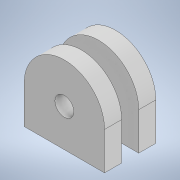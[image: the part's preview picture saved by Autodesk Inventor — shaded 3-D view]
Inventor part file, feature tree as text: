
AUTODESK INVENTOR PART (.ipt)
format: ipt  version: 2021 (Build 250183000, 183)  size: 118,784 bytes
history: native  units: mm
features: plane x2, extrude x1, mirror x1, sketch x1
ambient origin geometry x8: Origin, YZ Plane, XZ Plane, XY Plane, X Axis, Y Axis, Z Axis, Center Point
bodies: Solid1 (feature_tree)
feature tree (5):
  extrude  "Extrusion1"  Depth=10.0mm
  plane  "Work Plane1"
  mirror  "Mirror1"
  plane  "Work Plane2"
  sketch  "Sketch1"  dims[d0=11.0mm d1=18.0mm d2=18.0mm d3=22.0mm d4=90.0deg d5=10.0mm d6=1.0mm d7=0.0mm d8=0.0mm d11=5.0mm d12=0.0mm d17=0.5mm d18=0.872665mm d19=0.5mm d20=0.872665mm]
